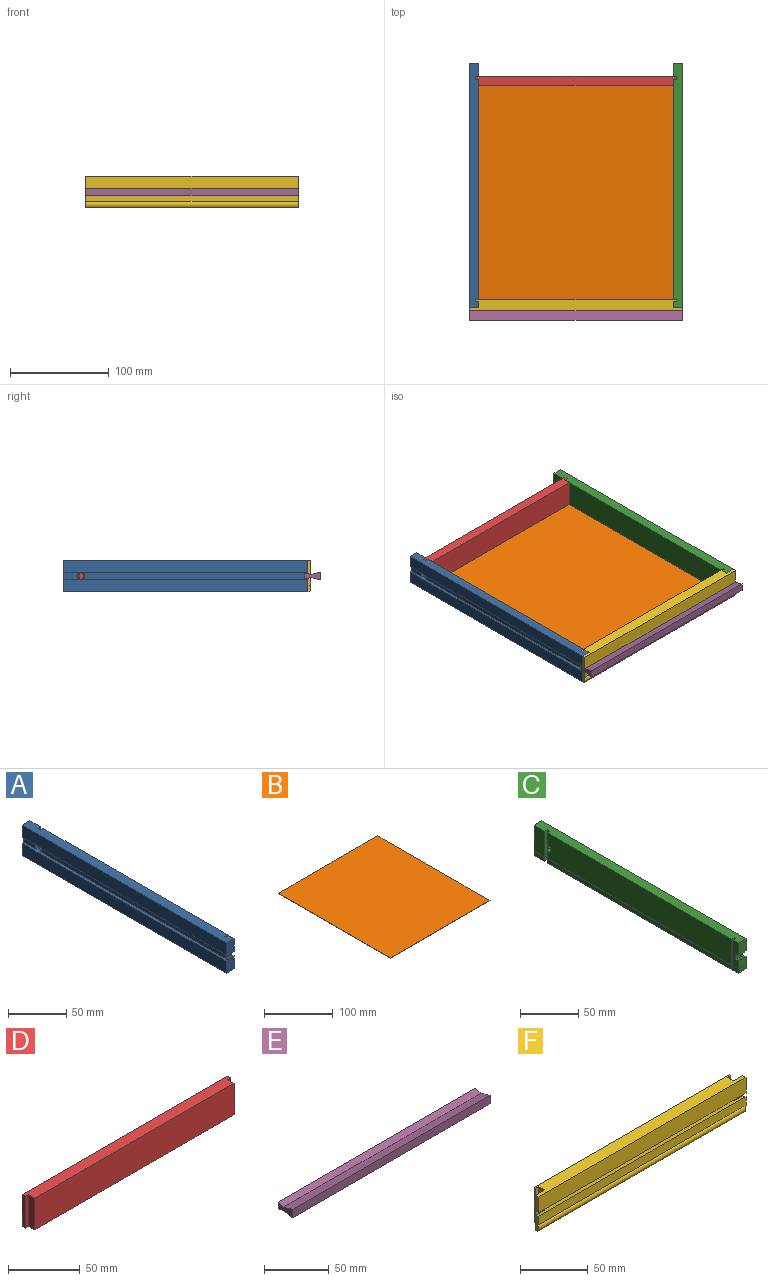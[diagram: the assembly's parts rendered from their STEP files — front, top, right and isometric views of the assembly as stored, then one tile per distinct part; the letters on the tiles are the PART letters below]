
ASSEMBLY  parts=6 mates=5
PART A: 43 faces, bbox 9.5x247.7x31.8 mm
  f0: plane 13.49x9.53mm, normal (0,-1,0), area 124.7mm2, adj f3,f6,f15,f16,f17,f32,f33,f34
  f1: plane 247.65x12.7mm, normal (-1,0,0), area 3142.6mm2, adj f2,f18,f20,f24,f37,f41
  f2: plane 13.49x9.53mm, normal (0,-1,0), area 126.6mm2, adj f1,f4,f15,f18,f36,f37
  f3: plane 7.14x3.18mm, normal (0,0.24,0.97), area 23.4mm2, adj f0,f5,f15,f38
  f4: plane 7.14x3.18mm, normal (0,0.24,-0.97), area 23.4mm2, adj f2,f5,f15,f36
  f5: plane 7.14x6.35mm, normal (0,-1,0), area 45.4mm2, adj f3,f4,f15,f35
  f6: plane 6.35x4.36mm, normal (1,0,0), area 27.7mm2, adj f0,f17,f29,f32
  f7: plane 223.84x4.36mm, normal (1,0,0), area 975.1mm2, adj f17,f25,f31,f32
  f8: plane 12.7x4.36mm, normal (1,0,0), area 55.3mm2, adj f17,f20,f26,f32
  f9: plane 8.36x3.18mm, normal (0,1,0), area 26.6mm2, adj f11,f19,f22,f33
  f10: plane 26.99x3.18mm, normal (0,-1,0), area 85.7mm2, adj f11,f18,f21,f33
  f11: plane 26.99x3.18mm, normal (1,0,0), area 79.5mm2, adj f9,f10,f18,f22,f27,f33
  f12: plane 26.99x3.18mm, normal (0,1,0), area 85.7mm2, adj f13,f15,f18,f33
  f13: plane 26.99x1.59mm, normal (1,0,0), area 42.8mm2, adj f12,f14,f18,f33
  f14: plane 26.99x3.18mm, normal (0,-1,0), area 85.7mm2, adj f13,f18,f19,f33
  f15: plane 26.99x6.35mm, normal (1,0,0), area 153.7mm2, adj f0,f2,f3,f4,f5,f12,f18,f33
  f16: plane 247.65x12.7mm, normal (-1,0,0), area 3142.6mm2, adj f0,f17,f20,f24,f39,f42
  f17: plane 247.65x9.53mm, normal (0,0,-1), area 2343.7mm2, adj f0,f6,f7,f8,f16,f20,f25,f26
  f18: plane 247.65x9.53mm, normal (0,0,1), area 2343.7mm2, adj f1,f2,f10,f11,f12,f13,f14,f15
  f19: plane 223.84x26.99mm, normal (1,0,0), area 6015.3mm2, adj f9,f14,f18,f22,f27,f33
  f20: plane 31.75x9.53mm, normal (0,1,0), area 285.4mm2, adj f1,f8,f16,f17,f18,f21,f32,f33
  f21: plane 26.99x12.7mm, normal (1,0,0), area 342.7mm2, adj f10,f18,f20,f33
  f22: cylinder r=3.17mm len=6.35mm, axis (-1,0,0), area 73.9mm2, adj f9,f11,f19,f23,f27
  f23: plane 7.94x7.94mm, normal (-1,0,0), area 17.8mm2, adj f22,f24
  f24: cylinder r=3.97mm len=7.94mm, axis (-1,0,0), area 83.7mm2, adj f1,f16,f23,f35,f37,f39,f40,f41
  f25: plane 4.36x3.18mm, normal (0,1,0), area 13.8mm2, adj f7,f17,f28,f32
  f26: plane 4.36x3.18mm, normal (0,-1,0), area 13.8mm2, adj f8,f17,f28,f32
  f27: plane 13.13x3.18mm, normal (0,1,0), area 41.7mm2, adj f11,f18,f19,f22
  f28: plane 4.36x3.18mm, normal (1,0,0), area 13.8mm2, adj f17,f25,f26,f32
  f29: plane 4.36x3.18mm, normal (0,1,0), area 13.8mm2, adj f6,f17,f30,f32
  f30: plane 4.36x1.59mm, normal (1,0,0), area 6.9mm2, adj f17,f29,f31,f32
  f31: plane 4.36x3.18mm, normal (0,-1,0), area 13.8mm2, adj f7,f17,f30,f32
  f32: plane 247.65x4.76mm, normal (0,0,1), area 1164.3mm2, adj f0,f6,f7,f8,f20,f25,f26,f28
  f33: plane 247.65x4.76mm, normal (0,0,-1), area 1164.3mm2, adj f0,f9,f10,f11,f12,f13,f14,f15
  f34: plane 247.65x0.41mm, normal (1,0,0), area 100.6mm2, adj f0,f20,f32,f33
  f35: plane 224.63x6.35mm, normal (-1,0,0), area 1419.4mm2, adj f5,f24,f37,f39
  f36: plane 3.18x0.79mm, normal (-1,0,0), area 1.3mm2, adj f2,f4,f37
  f37: plane 227.81x2.38mm, normal (0,0,-1), area 542.5mm2, adj f1,f2,f24,f35,f36
  f38: plane 3.18x0.79mm, normal (-1,0,0), area 1.3mm2, adj f0,f3,f39
  f39: plane 227.81x2.38mm, normal (0,0,1), area 542.5mm2, adj f0,f16,f24,f35,f38
  f40: plane 15.08x6.35mm, normal (-1,0,0), area 88.7mm2, adj f20,f24,f41,f42
  f41: plane 15.08x2.38mm, normal (0,0,-1), area 35.9mm2, adj f1,f20,f24,f40
  f42: plane 15.08x2.38mm, normal (0,0,1), area 35.9mm2, adj f16,f20,f24,f40
PART B: 6 faces, bbox 204.8x230.2x0.4 mm
  f0: plane 230.2x0.4mm, normal (1,0,0), area 91.4mm2, adj f1,f3,f4,f5
  f1: plane 204.8x0.4mm, normal (0,1,0), area 81.3mm2, adj f0,f2,f4,f5
  f2: plane 230.2x0.4mm, normal (-1,0,0), area 91.4mm2, adj f1,f3,f4,f5
  f3: plane 204.8x0.4mm, normal (0,-1,0), area 81.3mm2, adj f0,f2,f4,f5
  f4: plane 230.2x204.8mm, normal (0,0,-1), area 47145mm2, adj f0,f1,f2,f3
  f5: plane 230.2x204.8mm, normal (0,0,1), area 47145mm2, adj f0,f1,f2,f3
PART C: 43 faces, bbox 9.5x247.7x31.8 mm
  f0: plane 13.49x9.53mm, normal (0,-1,0), area 124.7mm2, adj f3,f6,f15,f16,f17,f32,f33,f34
  f1: plane 247.65x12.7mm, normal (1,0,0), area 3142.6mm2, adj f2,f18,f20,f24,f37,f41
  f2: plane 13.49x9.53mm, normal (0,-1,0), area 126.6mm2, adj f1,f4,f15,f18,f36,f37
  f3: plane 7.14x3.18mm, normal (0,0.24,0.97), area 23.4mm2, adj f0,f5,f15,f38
  f4: plane 7.14x3.18mm, normal (0,0.24,-0.97), area 23.4mm2, adj f2,f5,f15,f36
  f5: plane 7.14x6.35mm, normal (0,-1,0), area 45.4mm2, adj f3,f4,f15,f35
  f6: plane 6.35x4.36mm, normal (-1,0,0), area 27.7mm2, adj f0,f17,f29,f32
  f7: plane 223.84x4.36mm, normal (-1,0,0), area 975.1mm2, adj f17,f25,f31,f32
  f8: plane 12.7x4.36mm, normal (-1,0,0), area 55.3mm2, adj f17,f20,f26,f32
  f9: plane 8.36x3.18mm, normal (0,1,0), area 26.6mm2, adj f11,f19,f22,f33
  f10: plane 26.99x3.18mm, normal (0,-1,0), area 85.7mm2, adj f11,f18,f21,f33
  f11: plane 26.99x3.18mm, normal (-1,0,0), area 79.5mm2, adj f9,f10,f18,f22,f27,f33
  f12: plane 26.99x3.18mm, normal (0,1,0), area 85.7mm2, adj f13,f15,f18,f33
  f13: plane 26.99x1.59mm, normal (-1,0,0), area 42.8mm2, adj f12,f14,f18,f33
  f14: plane 26.99x3.18mm, normal (0,-1,0), area 85.7mm2, adj f13,f18,f19,f33
  f15: plane 26.99x6.35mm, normal (-1,0,0), area 153.7mm2, adj f0,f2,f3,f4,f5,f12,f18,f33
  f16: plane 247.65x12.7mm, normal (1,0,0), area 3142.6mm2, adj f0,f17,f20,f24,f39,f42
  f17: plane 247.65x9.53mm, normal (0,0,-1), area 2343.7mm2, adj f0,f6,f7,f8,f16,f20,f25,f26
  f18: plane 247.65x9.53mm, normal (0,0,1), area 2343.7mm2, adj f1,f2,f10,f11,f12,f13,f14,f15
  f19: plane 223.84x26.99mm, normal (-1,0,0), area 6015.3mm2, adj f9,f14,f18,f22,f27,f33
  f20: plane 31.75x9.53mm, normal (0,1,0), area 285.4mm2, adj f1,f8,f16,f17,f18,f21,f32,f33
  f21: plane 26.99x12.7mm, normal (-1,0,0), area 342.7mm2, adj f10,f18,f20,f33
  f22: cylinder r=3.17mm len=6.35mm, axis (1,0,0), area 73.9mm2, adj f9,f11,f19,f23,f27
  f23: plane 7.94x7.94mm, normal (1,0,0), area 17.8mm2, adj f22,f24
  f24: cylinder r=3.97mm len=7.94mm, axis (1,0,0), area 83.7mm2, adj f1,f16,f23,f35,f37,f39,f40,f41
  f25: plane 4.36x3.18mm, normal (0,1,0), area 13.8mm2, adj f7,f17,f28,f32
  f26: plane 4.36x3.18mm, normal (0,-1,0), area 13.8mm2, adj f8,f17,f28,f32
  f27: plane 13.13x3.18mm, normal (0,1,0), area 41.7mm2, adj f11,f18,f19,f22
  f28: plane 4.36x3.18mm, normal (-1,0,0), area 13.8mm2, adj f17,f25,f26,f32
  f29: plane 4.36x3.18mm, normal (0,1,0), area 13.8mm2, adj f6,f17,f30,f32
  f30: plane 4.36x1.59mm, normal (-1,0,0), area 6.9mm2, adj f17,f29,f31,f32
  f31: plane 4.36x3.18mm, normal (0,-1,0), area 13.8mm2, adj f7,f17,f30,f32
  f32: plane 247.65x4.76mm, normal (0,0,1), area 1164.3mm2, adj f0,f6,f7,f8,f20,f25,f26,f28
  f33: plane 247.65x4.76mm, normal (0,0,-1), area 1164.3mm2, adj f0,f9,f10,f11,f12,f13,f14,f15
  f34: plane 247.65x0.41mm, normal (-1,0,0), area 100.6mm2, adj f0,f20,f32,f33
  f35: plane 224.63x6.35mm, normal (1,0,0), area 1419.4mm2, adj f5,f24,f37,f39
  f36: plane 3.18x0.79mm, normal (1,0,0), area 1.3mm2, adj f2,f4,f37
  f37: plane 227.81x2.38mm, normal (0,0,-1), area 542.5mm2, adj f1,f2,f24,f35,f36
  f38: plane 3.18x0.79mm, normal (1,0,0), area 1.3mm2, adj f0,f3,f39
  f39: plane 227.81x2.38mm, normal (0,0,1), area 542.5mm2, adj f0,f16,f24,f35,f38
  f40: plane 15.08x6.35mm, normal (1,0,0), area 88.7mm2, adj f20,f24,f41,f42
  f41: plane 15.08x2.38mm, normal (0,0,-1), area 35.9mm2, adj f1,f20,f24,f40
  f42: plane 15.08x2.38mm, normal (0,0,1), area 35.9mm2, adj f16,f20,f24,f40
PART D: 10 faces, bbox 203.2x9.5x27 mm
  f0: plane 27x6.35mm, normal (1,0,0), area 171.5mm2, adj f1,f3,f5,f6
  f1: plane 203.2x9.53mm, normal (0,0,1), area 1895.2mm2, adj f0,f2,f4,f5,f6,f7,f8,f9
  f2: plane 27x6.35mm, normal (-1,0,0), area 171.5mm2, adj f1,f3,f5,f9
  f3: plane 203.2x9.53mm, normal (0,0,-1), area 1895.2mm2, adj f0,f2,f4,f5,f6,f7,f8,f9
  f4: plane 203.2x27mm, normal (0,1,0), area 5486.4mm2, adj f1,f3,f7,f8
  f5: plane 196.85x27mm, normal (0,-1,0), area 5315mm2, adj f0,f1,f2,f3
  f6: plane 27x3.18mm, normal (0,-1,0), area 85.7mm2, adj f0,f1,f3,f7
  f7: plane 27x3.18mm, normal (1,0,0), area 85.7mm2, adj f1,f3,f4,f6
  f8: plane 27x3.18mm, normal (-1,0,0), area 85.7mm2, adj f1,f3,f4,f9
  f9: plane 27x3.18mm, normal (0,-1,0), area 85.7mm2, adj f1,f2,f3,f8
PART E: 8 faces, bbox 215.9x15.9x7.9 mm
  f0: plane 215.9x6.35mm, normal (0,1,0), area 1371mm2, adj f1,f5,f6,f7
  f1: plane 215.9x6.35mm, normal (0,-0.24,0.97), area 1412.9mm2, adj f0,f2,f6,f7
  f2: plane 215.9x9.53mm, normal (0,0.24,0.97), area 2119.4mm2, adj f1,f3,f6,f7
  f3: plane 215.9x7.93mm, normal (0,-1,0), area 1712.8mm2, adj f2,f4,f6,f7
  f4: plane 215.9x9.53mm, normal (0,0.24,-0.97), area 2119.4mm2, adj f3,f5,f6,f7
  f5: plane 215.9x6.35mm, normal (0,-0.24,-0.97), area 1412.9mm2, adj f0,f4,f6,f7
  f6: plane 15.88x7.93mm, normal (1,0,0), area 83.2mm2, adj f0,f1,f2,f3,f4,f5
  f7: plane 15.88x7.93mm, normal (-1,0,0), area 83.2mm2, adj f0,f1,f2,f3,f4,f5
PART F: 32 faces, bbox 215.9x11.1x31.8 mm
  f0: plane 14.28x3.18mm, normal (-1,0,0), area 40.7mm2, adj f1,f6,f15,f23,f30,f31
  f1: plane 215.9x9.53mm, normal (0,0,-1), area 1915.3mm2, adj f0,f3,f4,f16,f18,f20,f22,f23
  f2: plane 203.2x26.99mm, normal (0,1,0), area 5483.9mm2, adj f5,f10,f19,f28
  f3: plane 203.2x4.36mm, normal (0,1,0), area 885.2mm2, adj f1,f9,f18,f27
  f4: plane 14.28x3.18mm, normal (1,0,0), area 40.7mm2, adj f1,f6,f15,f16,f30,f31
  f5: plane 215.9x11.11mm, normal (0,0,1), area 2258.1mm2, adj f2,f12,f13,f14,f17,f19,f21,f22
  f6: plane 215.9x6.35mm, normal (0,0.24,0.97), area 1350.6mm2, adj f0,f4,f7,f15,f16,f22,f23,f29
  f7: plane 196.85x6.35mm, normal (0,-1,0), area 1250mm2, adj f6,f8,f22,f29
  f8: plane 215.9x6.35mm, normal (0,0.24,-0.97), area 1350.6mm2, adj f7,f12,f13,f14,f17,f22,f24,f29
  f9: plane 203.2x4.76mm, normal (0,0,1), area 947.6mm2, adj f3,f11,f18,f20,f22,f25,f27,f29
  f10: plane 203.2x4.76mm, normal (0,0,-1), area 947.6mm2, adj f2,f11,f19,f21,f22,f26,f28,f29
  f11: plane 196.85x0.41mm, normal (0,1,0), area 80mm2, adj f9,f10,f22,f29
  f12: plane 14.28x3.18mm, normal (-1,0,0), area 44.1mm2, adj f5,f8,f13,f24
  f13: plane 215.9x14.28mm, normal (0,-1,0), area 3083.8mm2, adj f5,f8,f12,f14
  f14: plane 14.28x3.18mm, normal (1,0,0), area 44.1mm2, adj f5,f8,f13,f17
  f15: plane 215.9x7.72mm, normal (0,-1,0), area 1666.8mm2, adj f0,f4,f6,f31
  f16: plane 13.49x9.53mm, normal (0,1,0), area 128.5mm2, adj f1,f4,f6,f22
  f17: plane 13.49x9.53mm, normal (0,1,0), area 128.5mm2, adj f5,f8,f14,f22
  f18: plane 4.36x1.59mm, normal (1,0,0), area 6.9mm2, adj f1,f3,f9,f20
  f19: plane 26.99x1.59mm, normal (1,0,0), area 42.8mm2, adj f2,f5,f10,f21
  f20: plane 4.36x3.18mm, normal (0,-1,0), area 13.8mm2, adj f1,f9,f18,f22
  f21: plane 26.99x3.18mm, normal (0,-1,0), area 85.7mm2, adj f5,f10,f19,f22
  f22: plane 31.75x6.35mm, normal (1,0,0), area 182.7mm2, adj f1,f5,f6,f7,f8,f9,f10,f11
  f23: plane 13.49x9.53mm, normal (0,1,0), area 128.5mm2, adj f0,f1,f6,f29
  f24: plane 13.49x9.53mm, normal (0,1,0), area 128.5mm2, adj f5,f8,f12,f29
  f25: plane 4.36x3.18mm, normal (0,-1,0), area 13.8mm2, adj f1,f9,f27,f29
  f26: plane 26.99x3.18mm, normal (0,-1,0), area 85.7mm2, adj f5,f10,f28,f29
  f27: plane 4.36x1.59mm, normal (-1,0,0), area 6.9mm2, adj f1,f3,f9,f25
  f28: plane 26.99x1.59mm, normal (-1,0,0), area 42.8mm2, adj f2,f5,f10,f26
  f29: plane 31.75x6.35mm, normal (-1,0,0), area 182.7mm2, adj f1,f5,f6,f7,f8,f9,f10,f11
  f30: cylinder r=3.97mm len=215.9mm, axis (1,0,0), area 1671.1mm2, adj f0,f1,f4,f31
  f31: plane 215.9x1.9mm, normal (0,0,-1), area 410.5mm2, adj f0,f4,f15,f30
PLACE A t=(73.95,-75.25,28.86)mm
PLACE B t=(29.5,44.6,109.81)mm
PLACE C t=(137.45,-75.25,28.86)mm
PLACE D t=(29.5,-154.62,47.11)mm
PLACE E t=(29.5,-78.42,44.73)mm
PLACE F t=(29.5,-78.42,44.73)mm
MATE fastened E.f0 <-> F.f7  axis (0,1,0) through (29.5,-72.07,44.73)mm
MATE fastened A.f18 <-> F.f5  axis (0,0,1) through (-68.93,-72.07,60.61)mm
MATE fastened C.f18 <-> F.f5  axis (0,0,1) through (127.92,-72.07,60.61)mm
MATE fastened B.f5 <-> D.f3  axis (0,0,1) through (29.5,159.7,33.61)mm
MATE fastened D.f1 <-> A.f18  axis (0,0,1) through (-68.93,156.53,60.61)mm
